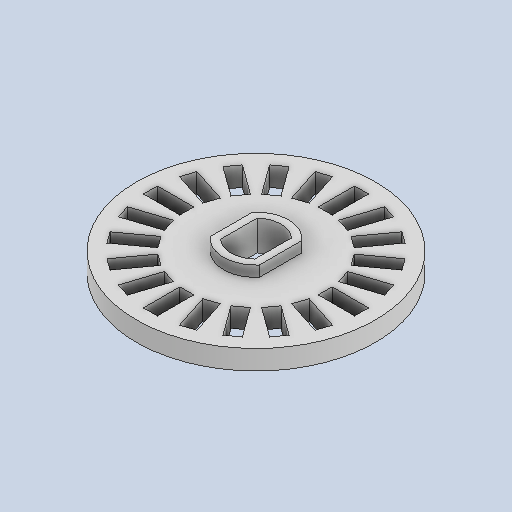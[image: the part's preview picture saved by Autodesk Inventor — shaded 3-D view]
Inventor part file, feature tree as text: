
AUTODESK INVENTOR PART (.ipt)
format: ipt  version: 2022 (Build 260153070, 153G)  size: 246,272 bytes
history: native  units: in
note: dims shown in document units (in); Inventor stores cm internally (conversion verified against a paired STEP export)
features: extrude x2, sketch x2
ambient origin geometry x8: Origin, YZ Plane, XZ Plane, XY Plane, X Axis, Y Axis, Z Axis, Center Point
bodies: Solid1 (feature_tree)
feature tree (4):
  extrude  "Extrusion1"  Depth=0.2126in
  extrude  "Extrusion2"  Depth=0.0453in
  sketch  "Sketch1"  dims[d0=1.0138in d1=0.2126in]
  sketch  "Sketch2"  dims[d3=0.1457in d4=0.187in d5=0.0591in d6=0.0591in d7=7.874in d9=360.0deg d11=0.0827in d12=0.0in d13=0.0315in d14=0.0315in d15=0.0315in d16=0.0453in d17=0.0in]
